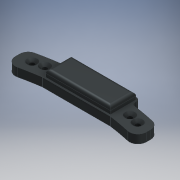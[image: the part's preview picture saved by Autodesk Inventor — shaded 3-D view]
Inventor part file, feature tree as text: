
AUTODESK INVENTOR PART (.ipt)
format: ipt  version: 2018 (Build 220112000, 112)  size: 166,912 bytes
history: native  units: mm
features: extrude x2, sketch x2, hole x1, mirror x1, fillet x1
ambient origin geometry x8: Origin, YZ Plane, XZ Plane, XY Plane, X Axis, Y Axis, Z Axis, Center Point
bodies: Solid1 (feature_tree)
feature tree (7):
  extrude  "Extrusion1"  Depth=77.0mm
  sketch  "Sketch2"  dims[d6=38.5mm d9=5.0mm d10=2.0mm d11=5.0mm d12=0.0mm d13=38.0mm d14=15.0mm d15=1.0mm d16=25.0mm d17=31.0mm d18=3.0mm d19=3.0mm d20=5.0mm d21=1.5mm d22=4.0mm d23=0.0mm d24=3.0mm d25=6.0mm d26=6.0mm d27=2.0mm d28=90.0deg d29=8.0mm d30=20.594885mm d31=2.0mm]
  extrude  "Extrusion2"  Depth=5.0mm
  hole  "Hole1"  [1 undecoded]
  mirror  "Mirror1"
  fillet  "Fillet1"  Radius=5.0mm
  sketch  "Sketch1"  dims[d0=245.0mm d1=10.0mm d3=4.5mm d5=77.0mm]
note: 1 required parameter value undecoded (feature->parameter linkage not recoverable at this tier; creation-order binding heuristic only, values carry confidence <= 0.55)
